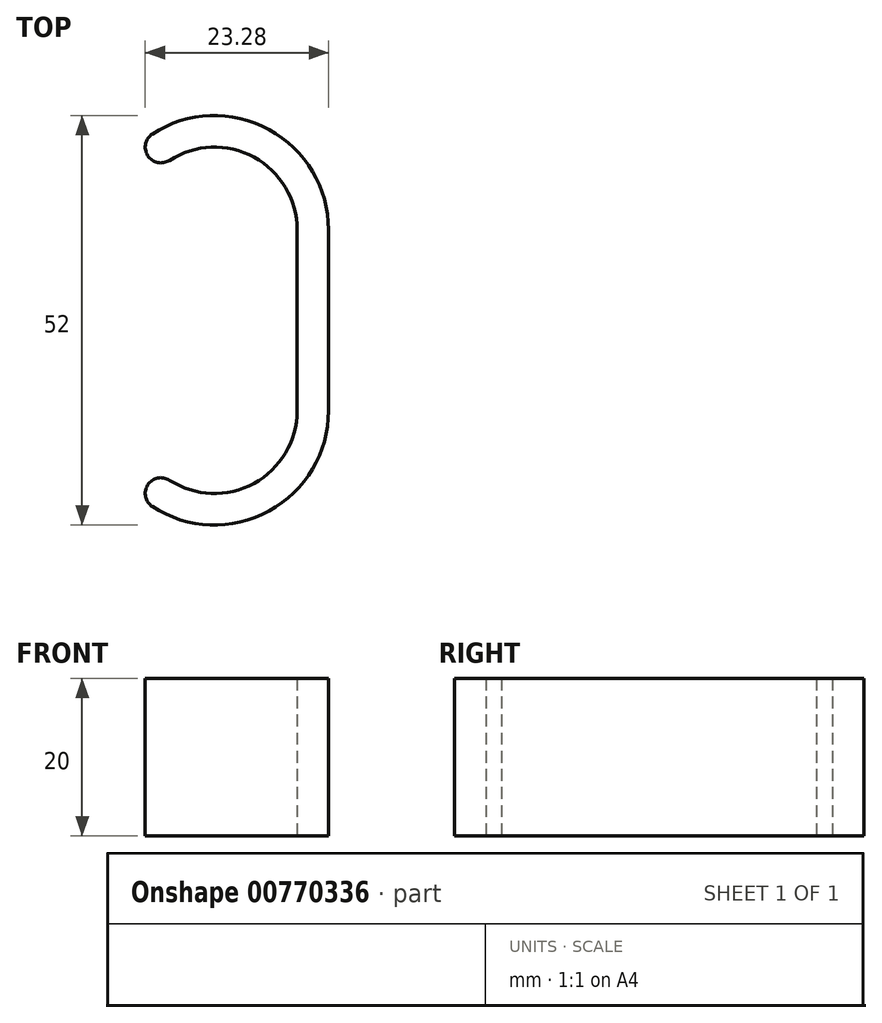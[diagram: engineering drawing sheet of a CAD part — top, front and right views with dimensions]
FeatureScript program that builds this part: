
annotation { "Feature Type Name" : "Feature", "Feature Type Description" : "" }
export const myFeature = defineFeature(function(context is Context, id is Id, definition is map)
    precondition{}
    {
        {
            var Q0;
            Q0=qCreatedBy(makeId("Top.planeOp"),FACE);
            var sketch = newSketch(context, id + "F0", { "sketchPlane" : qUnion([Q0])});
            skLineSegment(sketch, "E0.left", {"start": v(10.5, 11.5) * mm, "end": v(10.5, -11.5) * mm});
            skLineSegment(sketch, "E0.right", {"start": v(-10.5, 11.5) * mm, "end": v(-10.5, -11.5) * mm});
            skPoint(sketch, "E0.middle", {"position": v(0, 0) * mm});
            skArc(sketch, "E1", {"start": v(10.5, 11.5) * mm, "mid": v(0, 22) * mm, "end": v(-10.5, 11.5) * mm});
            skArc(sketch, "E2", {"start": v(-10.5, -11.5) * mm, "mid": v(0, -22) * mm, "end": v(10.5, -11.5) * mm});
            skPoint(sketch, "E3", {"position": v(0, 22) * mm});
            skLineSegment(sketch, "E4", {"start": v(0, 0) * mm, "end": v(10.5, 0) * mm, "construction": true});
            skLineSegment(sketch, "E5", {"start": v(0, 0) * mm, "end": v(0, 22) * mm, "construction": true});
            skLineSegment(sketch, "E6.0", {"start": v(-14.5, 11.5) * mm, "end": v(-14.5, -11.5) * mm});
            skArc(sketch, "E6.1", {"start": v(14.5, 11.5) * mm, "mid": v(0, 26) * mm, "end": v(-14.5, 11.5) * mm});
            skLineSegment(sketch, "E6.2", {"start": v(14.5, 11.5) * mm, "end": v(14.5, -11.5) * mm});
            skArc(sketch, "E6.3", {"start": v(-14.5, -11.5) * mm, "mid": v(0, -26) * mm, "end": v(14.5, -11.5) * mm});
            skArc(sketch, "E7", {"start": v(-7.87, 23.68) * mm, "mid": v(-8.46, 20.91) * mm, "end": v(-5.7, 20.32) * mm});
            skPoint(sketch, "E8", {"position": v(-6.78, 20) * mm});
            skArc(sketch, "E9.MirrorCS", {"start": v(-7.87, -23.68) * mm, "mid": v(-8.46, -20.91) * mm, "end": v(-5.7, -20.32) * mm});
            skSolve(sketch);
        }
        {
            var Q0;
            {var subQ4=sQuery(id+"F0.wireOp",EDGE,"E0.left");Q0=makeQuery(id+"F0.imprint","IMPRINT",FACE,{"disambiguationData":[TD([[makeQuery(id+"F0.imprint","IMPRINT",EDGE,{"derivedFrom":subQ4}),1.0]])]});}
            extrude(context, id + "F1", {"entities" : qUnion([Q0]), "depth" : 20 * mm, "offsetDistance" : 25 * mm});
        }
    });
